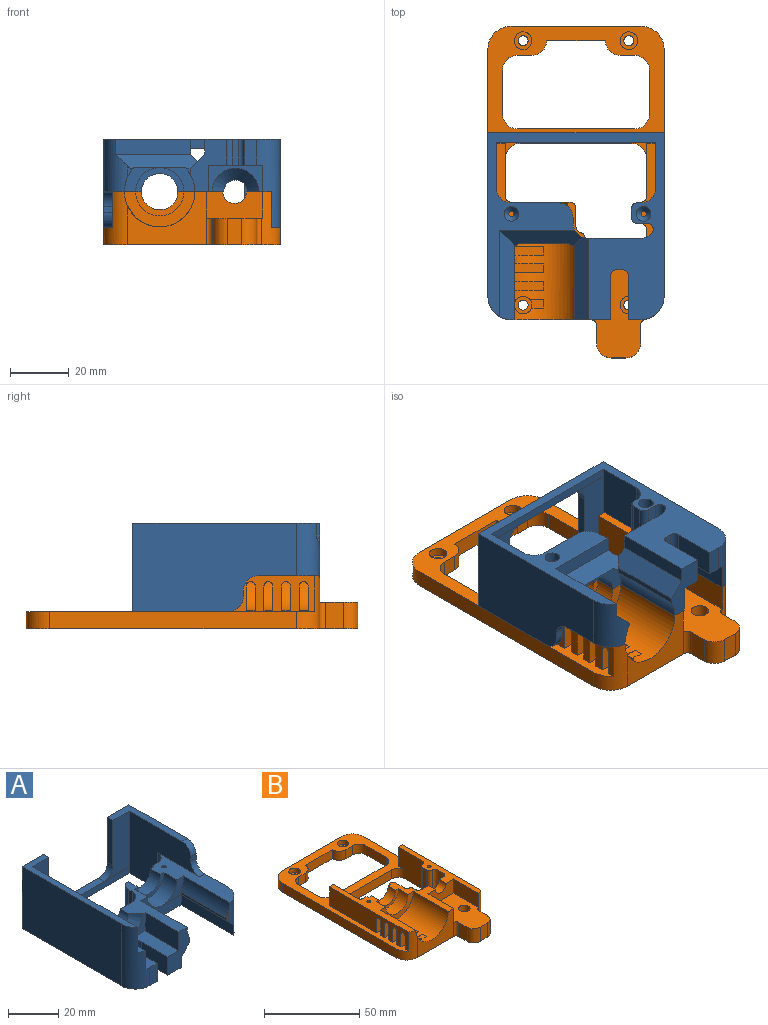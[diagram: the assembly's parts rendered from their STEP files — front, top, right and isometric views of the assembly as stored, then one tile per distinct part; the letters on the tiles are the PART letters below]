
ASSEMBLY  parts=2 mates=1
PART A: 76 faces, bbox 60x63.6x30 mm
  f0: plane 63.6x60mm, normal (0,0,-1), area 1352mm2, adj f4,f5,f6,f10,f11,f17,f21,f29
  f1: plane 54.2x3.2mm, normal (0,0,1), area 88.8mm2, adj f6,f21,f60,f61,f63,f65,f66,f67
  f2: plane 32.6x12mm, normal (0,0,1), area 121.8mm2, adj f4,f21,f52,f60,f61,f62
  f3: plane 61.76x12mm, normal (0,0,1), area 201mm2, adj f5,f6,f38,f60,f63,f64
  f4: plane 55.6x30mm, normal (1,0,0), area 1448.4mm2, adj f0,f2,f10,f20,f50,f51,f52,f60
  f5: plane 55.6x30mm, normal (-1,0,0), area 1668mm2, adj f0,f3,f38,f60
  f6: plane 58.76x30mm, normal (1,0,0), area 999mm2, adj f0,f1,f3,f7,f38,f63,f65,f68
  f7: plane 44.47x8.3mm, normal (0,0,1), area 186.9mm2, adj f6,f9,f23,f24,f38,f39,f53,f54
  f8: plane 38.8x15.6mm, normal (0,0,1), area 205.3mm2, adj f9,f13,f17,f18,f19,f22,f23,f25
  f9: cylinder r=4mm len=8mm, axis (0,1,0), area 59.3mm2, adj f7,f8,f53,f54
  f10: cylinder r=8mm len=17.8mm, axis (0,0,1), area 191.3mm2, adj f0,f4,f15,f16,f20,f29,f36
  f11: plane 8.8x4.2mm, normal (0,-1,0), area 37mm2, adj f0,f12,f38,f47
  f12: plane 19x18.4mm, normal (0,0,1), area 249.1mm2, adj f11,f17,f23,f24,f25,f38,f45,f46
  f13: cylinder r=12mm len=26mm, axis (0,1,0), area 164.5mm2, adj f8,f14,f17,f22,f33,f37
  f14: plane 1.81x1.28mm, normal (0,-1,0), area 1.1mm2, adj f13,f33,f37
  f15: plane 4x1mm, normal (0,-1,0), area 2.5mm2, adj f10,f16,f32,f36
  f16: cylinder r=12mm len=26mm, axis (0,1,0), area 183.7mm2, adj f10,f15,f20,f22,f32,f34,f37
  f17: plane 17.8x12.4mm, normal (0,-1,0), area 120.9mm2, adj f0,f8,f12,f13,f25,f30,f33,f35
  f18: plane 16.4x8.2mm, normal (0,-1,0), area 45.2mm2, adj f8,f20,f26,f28
  f19: plane 16.09x8.2mm, normal (0,1,0), area 44.8mm2, adj f8,f20,f26,f27,f72
  f20: plane 44.66x12.8mm, normal (0,0,1), area 276.2mm2, adj f4,f10,f16,f18,f19,f21,f22,f26
  f21: plane 39.6x30mm, normal (-1,0,0), area 704.2mm2, adj f0,f1,f2,f20,f50,f51,f52,f61
  f22: plane 24x8.4mm, normal (0,-1,0), area 78mm2, adj f8,f13,f16,f20,f28,f37
  f23: plane 18.4x9mm, normal (0,-1,0), area 65.1mm2, adj f7,f8,f12,f24,f25,f53
  f24: plane 18.75x9mm, normal (1,0,0), area 168.7mm2, adj f7,f12,f23,f38
  f25: plane 19x9mm, normal (-1,0,0), area 171mm2, adj f8,f12,f17,f23
  f26: cylinder r=6.2mm len=12.4mm, axis (0,-1,0), area 109.1mm2, adj f8,f18,f19,f20
  f27: cylinder r=8.2mm len=16.09mm, axis (0,1,0), area 19.7mm2, adj f19,f20,f55,f72
  f28: cylinder r=8.2mm len=16.4mm, axis (0,-1,0), area 185.5mm2, adj f8,f18,f20,f22
  f29: plane 29.33x5mm, normal (-1,0,0), area 146.6mm2, adj f0,f10,f31,f36
  f30: plane 27.72x5mm, normal (1,0,0), area 138.6mm2, adj f0,f17,f35,f54
  f31: plane 25.57x5mm, normal (0,-1,0), area 127.9mm2, adj f0,f29,f37,f70
  f32: plane 25.4x1.17mm, normal (-1,0,0), area 29.6mm2, adj f15,f16,f34,f36
  f33: plane 25.4x1.81mm, normal (1,0,0), area 46.1mm2, adj f13,f14,f17,f35
  f34: plane 1.17x0.88mm, normal (0,-1,0), area 0.5mm2, adj f16,f32,f37
  f35: plane 28.1x5mm, normal (0.71,0,-0.71), area 192.6mm2, adj f17,f30,f33,f37,f54,f70
  f36: plane 30.4x5mm, normal (-0.71,0,-0.71), area 195.3mm2, adj f10,f15,f29,f32,f37
  f37: plane 28.11x5.01mm, normal (0,-0.71,-0.71), area 155.7mm2, adj f13,f14,f16,f22,f31,f34,f35,f36
  f38: cylinder r=8mm len=30mm, axis (0,0,-1), area 291.3mm2, adj f0,f3,f5,f6,f7,f11,f12,f24
  f39: cylinder r=0.9mm len=2mm, axis (0,0,1), area 11.3mm2, adj f7,f43
  f40: cylinder r=0.9mm len=2mm, axis (0,0,1), area 11.3mm2, adj f20,f44
  f41: cylinder r=2.5mm len=14.2mm, axis (0,0,-1), area 223.1mm2, adj f0,f44
  f42: cylinder r=2.5mm len=14.2mm, axis (0,0,-1), area 223.1mm2, adj f0,f43
  f43: cone r=0.9mm half-angle=45deg, axis (0,0,-1), area 24.2mm2, adj f39,f42
  f44: cone r=0.9mm half-angle=45deg, axis (0,0,-1), area 24.2mm2, adj f40,f41
  f45: plane 15x8.8mm, normal (-1,0,0), area 132mm2, adj f0,f12,f17,f48
  f46: plane 8.8x2mm, normal (0,-1,0), area 17.6mm2, adj f0,f12,f48,f49
  f47: plane 15x8.8mm, normal (1,0,0), area 132mm2, adj f0,f11,f12,f49
  f48: cylinder r=2mm len=8.8mm, axis (0,0,1), area 27.6mm2, adj f0,f12,f45,f46
  f49: cylinder r=2mm len=8.8mm, axis (0,0,-1), area 27.6mm2, adj f0,f12,f46,f47
  f50: plane 2.9x2.2mm, normal (0,-1,0), area 6.4mm2, adj f4,f21,f51,f52
  f51: cylinder r=5mm len=5mm, axis (1,0,0), area 22.8mm2, adj f4,f20,f21,f50
  f52: cylinder r=5mm len=5mm, axis (1,0,0), area 22.8mm2, adj f2,f4,f21,f50
  f53: cone r=8mm half-angle=45deg, axis (0,-1,0), area 106.6mm2, adj f7,f8,f9,f23
  f54: plane 18.1x17.8mm, normal (0,1,0), area 295mm2, adj f0,f7,f8,f9,f30,f35,f69,f70
  f55: plane 17.8x16.1mm, normal (0,1,0), area 195.5mm2, adj f0,f20,f27,f71,f72
  f56: plane 17.8x1.24mm, normal (0,1,0), area 22.1mm2, adj f0,f7,f68,f73
  f57: plane 17.8x3mm, normal (1,0,0), area 53.4mm2, adj f0,f7,f73,f74
  f58: plane 17.8x3.48mm, normal (0,-1,0), area 61.9mm2, adj f0,f7,f74,f75
  f59: plane 17.8x2mm, normal (-1,0,0), area 35.6mm2, adj f0,f8,f70,f72
  f60: plane 60x30mm, normal (0,1,0), area 838.7mm2, adj f0,f1,f2,f3,f4,f5,f62,f64
  f61: plane 27x14.1mm, normal (0,-1,0), area 251.1mm2, adj f1,f2,f21,f62,f67
  f62: plane 22x3mm, normal (-1,0,0), area 66mm2, adj f2,f60,f61,f67
  f63: plane 27x14.1mm, normal (0,-1,0), area 251.1mm2, adj f1,f3,f6,f64,f66
  f64: plane 22x3mm, normal (1,0,0), area 66mm2, adj f3,f60,f63,f66
  f65: plane 54.2x3mm, normal (0,-1,0), area 162.6mm2, adj f0,f1,f6,f21
  f66: cylinder r=5mm len=5mm, axis (0,-1,0), area 23.6mm2, adj f1,f60,f63,f64
  f67: cylinder r=5mm len=5mm, axis (0,1,0), area 23.6mm2, adj f1,f60,f61,f62
  f68: cylinder r=5mm len=17.8mm, axis (0,0,-1), area 139.8mm2, adj f0,f6,f7,f56
  f69: cylinder r=5mm len=17.8mm, axis (0,0,-1), area 74.9mm2, adj f0,f7,f54,f75
  f70: cylinder r=5mm len=17.8mm, axis (0,0,-1), area 105.4mm2, adj f0,f8,f31,f35,f37,f54,f59
  f71: cylinder r=5mm len=17.8mm, axis (0,0,-1), area 139.8mm2, adj f0,f20,f21,f55
  f72: cylinder r=5mm len=17.8mm, axis (0,0,-1), area 125mm2, adj f0,f8,f19,f27,f55,f59
  f73: cylinder r=2mm len=17.8mm, axis (0,0,-1), area 55.9mm2, adj f0,f7,f56,f57
  f74: cylinder r=2mm len=17.8mm, axis (0,0,1), area 55.9mm2, adj f0,f7,f57,f58
  f75: cylinder r=2mm len=17.8mm, axis (0,0,-1), area 81.9mm2, adj f0,f7,f58,f69
PART B: 107 faces, bbox 60x113x18 mm
  f0: plane 113x60mm, normal (0,0,-1), area 3475.5mm2, adj f5,f6,f7,f11,f15,f34,f35,f36
  f1: plane 98.25x60mm, normal (0,0,1), area 1488.1mm2, adj f2,f5,f6,f7,f8,f9,f10,f11
  f2: plane 12.2x3mm, normal (0,1,0), area 36.6mm2, adj f1,f3,f20,f81
  f3: plane 59.75x8.5mm, normal (0,0,1), area 234.8mm2, adj f2,f4,f11,f20,f22,f24,f68,f73
  f4: cylinder r=4mm len=8mm, axis (0,-1,0), area 65.1mm2, adj f3,f13,f22,f73
  f5: plane 44x5.8mm, normal (0,1,0), area 255.2mm2, adj f0,f1,f38,f40
  f6: plane 84x5.8mm, normal (-1,0,0), area 487.2mm2, adj f0,f1,f38,f39
  f7: plane 84x5.8mm, normal (1,0,0), area 487.2mm2, adj f0,f1,f11,f40
  f8: cylinder r=3mm len=8.12mm, axis (0,0,1), area 86.7mm2, adj f1,f12,f28,f47,f48,f49,f50,f51
  f9: cylinder r=3mm len=6mm, axis (0,0,1), area 52.8mm2, adj f1,f29
  f10: cylinder r=3mm len=6mm, axis (0,0,1), area 52.8mm2, adj f1,f30
  f11: cylinder r=8mm len=18mm, axis (0,0,-1), area 106.1mm2, adj f0,f1,f3,f7,f20,f24,f25,f60
  f12: cylinder r=12mm len=26mm, axis (0,1,0), area 767.6mm2, adj f8,f13,f15,f16,f18,f39,f41,f42
  f13: plane 40x15.3mm, normal (0,0,1), area 190.6mm2, adj f4,f12,f15,f17,f18,f21,f22,f23
  f14: plane 12.2x3mm, normal (0,1,0), area 36.6mm2, adj f1,f16,f19,f80
  f15: plane 27x18mm, normal (0,-1,0), area 263mm2, adj f0,f12,f13,f23,f39,f59
  f16: plane 59.94x9.8mm, normal (0,0,1), area 280mm2, adj f12,f14,f17,f18,f19,f21,f31,f32
  f17: plane 16.4x8.2mm, normal (0,1,0), area 45.2mm2, adj f13,f16,f31,f32
  f18: plane 24x12mm, normal (0,-1,0), area 120.6mm2, adj f12,f13,f16,f33
  f19: plane 58.25x12.2mm, normal (-1,0,0), area 592.1mm2, adj f1,f14,f16,f39,f41,f42,f43,f44
  f20: plane 58.25x12.2mm, normal (1,0,0), area 710.6mm2, adj f1,f2,f3,f11
  f21: plane 16.4x8.2mm, normal (0,-1,0), area 45.2mm2, adj f13,f16,f31,f33
  f22: plane 19x9mm, normal (0,-1,0), area 145.9mm2, adj f3,f4,f13,f23,f24,f25
  f23: plane 19x9mm, normal (1,0,0), area 171mm2, adj f13,f15,f22,f25
  f24: plane 18.75x9mm, normal (-1,0,0), area 168.7mm2, adj f3,f11,f22,f25
  f25: plane 32x19mm, normal (0,0,1), area 515.8mm2, adj f11,f22,f23,f24,f27,f56,f57,f58
  f26: plane 6x6mm, normal (0,0,1), area 19.2mm2, adj f27,f35
  f27: cylinder r=3mm len=6mm, axis (0,0,1), area 113.1mm2, adj f25,f26
  f28: plane 6x6mm, normal (0,0,1), area 19.2mm2, adj f8,f37
  f29: plane 6x6mm, normal (0,0,1), area 19.2mm2, adj f9,f36
  f30: plane 6x6mm, normal (0,0,1), area 19.2mm2, adj f10,f34
  f31: cylinder r=6.2mm len=12.4mm, axis (0,1,0), area 109.1mm2, adj f13,f16,f17,f21
  f32: cylinder r=8.2mm len=16.4mm, axis (0,1,0), area 30.9mm2, adj f13,f16,f17,f72
  f33: cylinder r=8.2mm len=16.4mm, axis (0,1,0), area 185.5mm2, adj f13,f16,f18,f21
  f34: cylinder r=1.7mm len=3.4mm, axis (0,0,1), area 32mm2, adj f0,f30
  f35: cylinder r=1.7mm len=3.4mm, axis (0,0,1), area 32mm2, adj f0,f26
  f36: cylinder r=1.7mm len=3.4mm, axis (0,0,1), area 32mm2, adj f0,f29
  f37: cylinder r=1.7mm len=3.4mm, axis (0,0,1), area 32mm2, adj f0,f28
  f38: cylinder r=8mm len=8mm, axis (0,0,1), area 72.9mm2, adj f0,f1,f5,f6
  f39: cylinder r=8mm len=18mm, axis (0,0,1), area 135.5mm2, adj f0,f1,f6,f12,f15,f16,f19
  f40: cylinder r=8mm len=8mm, axis (0,0,-1), area 72.9mm2, adj f0,f1,f5,f7
  f41: plane 16x8.7mm, normal (0,1,0), area 67.5mm2, adj f1,f12,f19,f52,f71
  f42: plane 16x8.7mm, normal (0,-1,0), area 67.5mm2, adj f1,f12,f19,f52,f71
  f43: plane 16x8.7mm, normal (0,1,0), area 67.5mm2, adj f1,f12,f19,f53,f70
  f44: plane 16x8.7mm, normal (0,-1,0), area 67.5mm2, adj f1,f12,f19,f53,f70
  f45: plane 16x8.7mm, normal (0,1,0), area 67.5mm2, adj f1,f12,f19,f54,f69
  f46: plane 16x8.7mm, normal (0,-1,0), area 67.5mm2, adj f1,f12,f19,f54,f69
  f47: plane 8.7x6.76mm, normal (0,-1,0), area 53.4mm2, adj f1,f8,f12,f19,f55
  f48: plane 8.7x6.17mm, normal (0,1,0), area 50.5mm2, adj f1,f8,f12,f19,f55
  f49: plane 4.17x0.75mm, normal (0,1,0), area 1mm2, adj f8,f12,f51
  f50: plane 4.76x0.99mm, normal (0,-1,0), area 1.5mm2, adj f8,f12,f51
  f51: plane 4.76x3mm, normal (0,0,1), area 12.5mm2, adj f8,f12,f49,f50
  f52: cylinder r=1.5mm len=4.52mm, axis (-1,0,0), area 20.2mm2, adj f12,f19,f41,f42
  f53: cylinder r=1.5mm len=4.52mm, axis (-1,0,0), area 20.2mm2, adj f12,f19,f43,f44
  f54: cylinder r=1.5mm len=4.52mm, axis (-1,0,0), area 20.2mm2, adj f12,f19,f45,f46
  f55: cylinder r=1.5mm len=4.52mm, axis (-1,0,0), area 20.2mm2, adj f12,f19,f47,f48
  f56: plane 9x6mm, normal (-1,0,0), area 54mm2, adj f0,f25,f59,f61
  f57: plane 9x6.2mm, normal (1,0,0), area 55.8mm2, adj f0,f25,f60,f62
  f58: plane 9x5mm, normal (0,-1,0), area 45mm2, adj f0,f25,f61,f62
  f59: cylinder r=2mm len=9mm, axis (0,0,-1), area 28.3mm2, adj f0,f15,f25,f56
  f60: cylinder r=2mm len=9mm, axis (0,0,-1), area 24.6mm2, adj f0,f11,f25,f57
  f61: cylinder r=5mm len=9mm, axis (0,0,1), area 70.7mm2, adj f0,f25,f56,f58
  f62: cylinder r=5mm len=9mm, axis (0,0,-1), area 70.7mm2, adj f0,f25,f57,f58
  f63: plane 1.8x1.8mm, normal (0,0,1), area 2.5mm2, adj f64
  f64: cylinder r=0.9mm len=7mm, axis (0,0,1), area 39.6mm2, adj f25,f63
  f65: plane 1.8x1.8mm, normal (0,0,1), area 2.5mm2, adj f66
  f66: cylinder r=0.9mm len=16mm, axis (0,0,1), area 90.5mm2, adj f16,f65
  f67: plane 1.8x1.8mm, normal (0,0,1), area 2.5mm2, adj f68
  f68: cylinder r=0.9mm len=16mm, axis (0,0,1), area 90.5mm2, adj f3,f67
  f69: plane 3x0.2mm, normal (-1,0,0), area 0.6mm2, adj f1,f12,f45,f46
  f70: plane 3x0.2mm, normal (-1,0,0), area 0.6mm2, adj f1,f12,f43,f44
  f71: plane 3x0.2mm, normal (-1,0,0), area 0.6mm2, adj f1,f12,f41,f42
  f72: plane 20x18mm, normal (0,1,0), area 254.4mm2, adj f0,f13,f16,f32,f83,f84
  f73: plane 18x16.91mm, normal (0,1,0), area 279.3mm2, adj f0,f3,f4,f13,f86,f87
  f74: plane 18x6.43mm, normal (1,0,0), area 115.7mm2, adj f0,f13,f84,f85
  f75: plane 18x1.5mm, normal (1,0,0), area 27mm2, adj f0,f13,f86,f92
  f76: plane 18x4.56mm, normal (-1,0,0), area 82.1mm2, adj f0,f3,f87,f88
  f77: plane 18x0.22mm, normal (0,-1,0), area 4mm2, adj f0,f3,f88,f89
  f78: plane 18x3.26mm, normal (-1,0,0), area 58.6mm2, adj f0,f3,f89,f90
  f79: plane 18x0.22mm, normal (0,1,0), area 4mm2, adj f0,f3,f90,f91
  f80: plane 18x18mm, normal (1,0,0), area 295mm2, adj f0,f1,f14,f16,f83,f105
  f81: plane 18x18mm, normal (-1,0,0), area 295mm2, adj f0,f1,f2,f3,f91,f106
  f82: plane 38x5.8mm, normal (0,-1,0), area 220.4mm2, adj f0,f1,f105,f106
  f83: cylinder r=2mm len=18mm, axis (0,0,-1), area 56.5mm2, adj f0,f16,f72,f80
  f84: cylinder r=2mm len=18mm, axis (0,0,-1), area 56.5mm2, adj f0,f13,f72,f74
  f85: cylinder r=2mm len=18mm, axis (0,0,-1), area 48.2mm2, adj f0,f13,f74,f92
  f86: cylinder r=2mm len=18mm, axis (0,0,1), area 56.5mm2, adj f0,f13,f73,f75
  f87: cylinder r=2mm len=18mm, axis (0,0,-1), area 56.5mm2, adj f0,f3,f73,f76
  f88: cylinder r=2mm len=18mm, axis (0,0,1), area 56.5mm2, adj f0,f3,f76,f77
  f89: cylinder r=2mm len=18mm, axis (0,0,1), area 56.5mm2, adj f0,f3,f77,f78
  f90: cylinder r=2mm len=18mm, axis (0,0,-1), area 56.5mm2, adj f0,f3,f78,f79
  f91: cylinder r=2mm len=18mm, axis (0,0,-1), area 56.5mm2, adj f0,f3,f79,f81
  f92: cylinder r=2mm len=18mm, axis (0,0,-1), area 48.2mm2, adj f0,f13,f75,f85
  f93: plane 40x5.8mm, normal (0,1,0), area 232mm2, adj f0,f1,f99,f103
  f94: plane 15x5.8mm, normal (-1,0,0), area 87mm2, adj f0,f1,f99,f100
  f95: plane 5.8x5mm, normal (0,-1,0), area 29mm2, adj f0,f1,f100,f101
  f96: plane 20x5.8mm, normal (0,-1,0), area 116mm2, adj f0,f1,f101,f102
  f97: plane 5.8x5mm, normal (0,-1,0), area 29mm2, adj f0,f1,f102,f104
  f98: plane 15x5.8mm, normal (1,0,0), area 87mm2, adj f0,f1,f103,f104
  f99: cylinder r=5mm len=5.8mm, axis (0,0,-1), area 45.6mm2, adj f0,f1,f93,f94
  f100: cylinder r=5mm len=5.8mm, axis (0,0,-1), area 45.6mm2, adj f0,f1,f94,f95
  f101: cylinder r=5mm len=5.8mm, axis (0,0,1), area 45.6mm2, adj f0,f1,f95,f96
  f102: cylinder r=5mm len=5.8mm, axis (0,0,1), area 45.6mm2, adj f0,f1,f96,f97
  f103: cylinder r=5mm len=5.8mm, axis (0,0,1), area 45.6mm2, adj f0,f1,f93,f98
  f104: cylinder r=5mm len=5.8mm, axis (0,0,-1), area 45.6mm2, adj f0,f1,f97,f98
  f105: cylinder r=5mm len=5.8mm, axis (0,0,1), area 45.6mm2, adj f0,f1,f80,f82
  f106: cylinder r=5mm len=5.8mm, axis (0,0,-1), area 45.6mm2, adj f0,f1,f81,f82
PLACE A rot(axis=(0,-1,0),180deg) t=(23.37,0,-40.56)mm
PLACE B t=(23.37,0,-76.36)mm
MATE fastened B.f68 <-> A.f39  axis (0,0,1) through (46.37,-14,-58.36)mm
